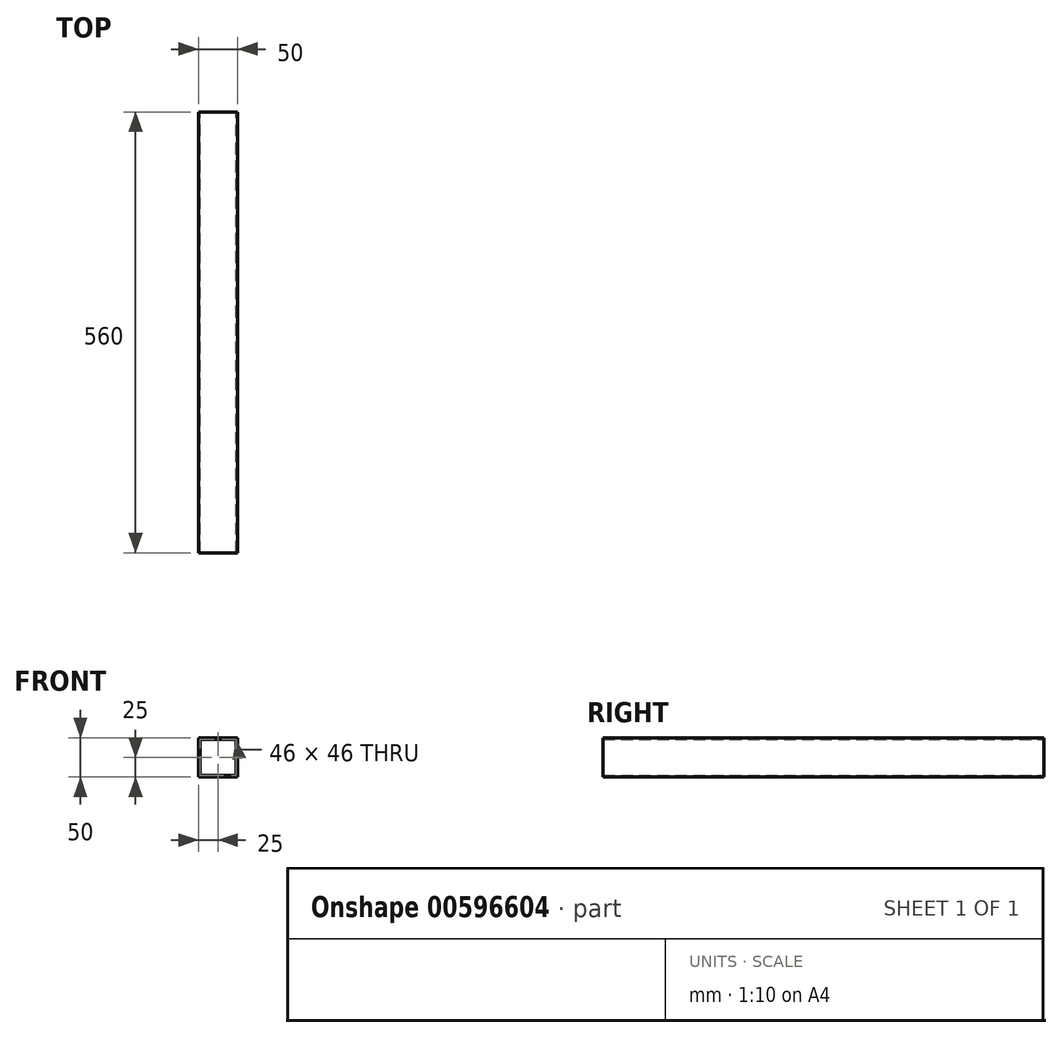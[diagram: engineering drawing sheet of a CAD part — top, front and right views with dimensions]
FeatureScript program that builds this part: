
annotation { "Feature Type Name" : "Feature", "Feature Type Description" : "" }
export const myFeature = defineFeature(function(context is Context, id is Id, definition is map)
    precondition{}
    {
        {
            var Q0;
            Q0=qCreatedBy(makeId("Front.planeOp"),FACE);
            var sketch = newSketch(context, id + "F0", { "sketchPlane" : qUnion([Q0])});
            skLineSegment(sketch, "E0.bottom", {"start": v(0, 0) * mm, "end": v(50, 0) * mm});
            skLineSegment(sketch, "E0.top", {"start": v(0, 50) * mm, "end": v(50, 50) * mm});
            skLineSegment(sketch, "E0.left", {"start": v(0, 0) * mm, "end": v(0, 50) * mm});
            skLineSegment(sketch, "E0.right", {"start": v(50, 0) * mm, "end": v(50, 50) * mm});
            skLineSegment(sketch, "E1.bottom", {"start": v(2, 2) * mm, "end": v(48, 2) * mm});
            skLineSegment(sketch, "E1.top", {"start": v(2, 48) * mm, "end": v(48, 48) * mm});
            skLineSegment(sketch, "E1.left", {"start": v(2, 2) * mm, "end": v(2, 48) * mm});
            skLineSegment(sketch, "E1.right", {"start": v(48, 2) * mm, "end": v(48, 48) * mm});
            skSolve(sketch);
        }
        {
            var Q0;
            Q0 = qSketchRegion(id + "F0", true);
            extrude(context, id + "F1", {"entities" : qUnion([Q0]), "depth" : 560 * mm, "offsetDistance" : 25 * mm});
        }
    });
